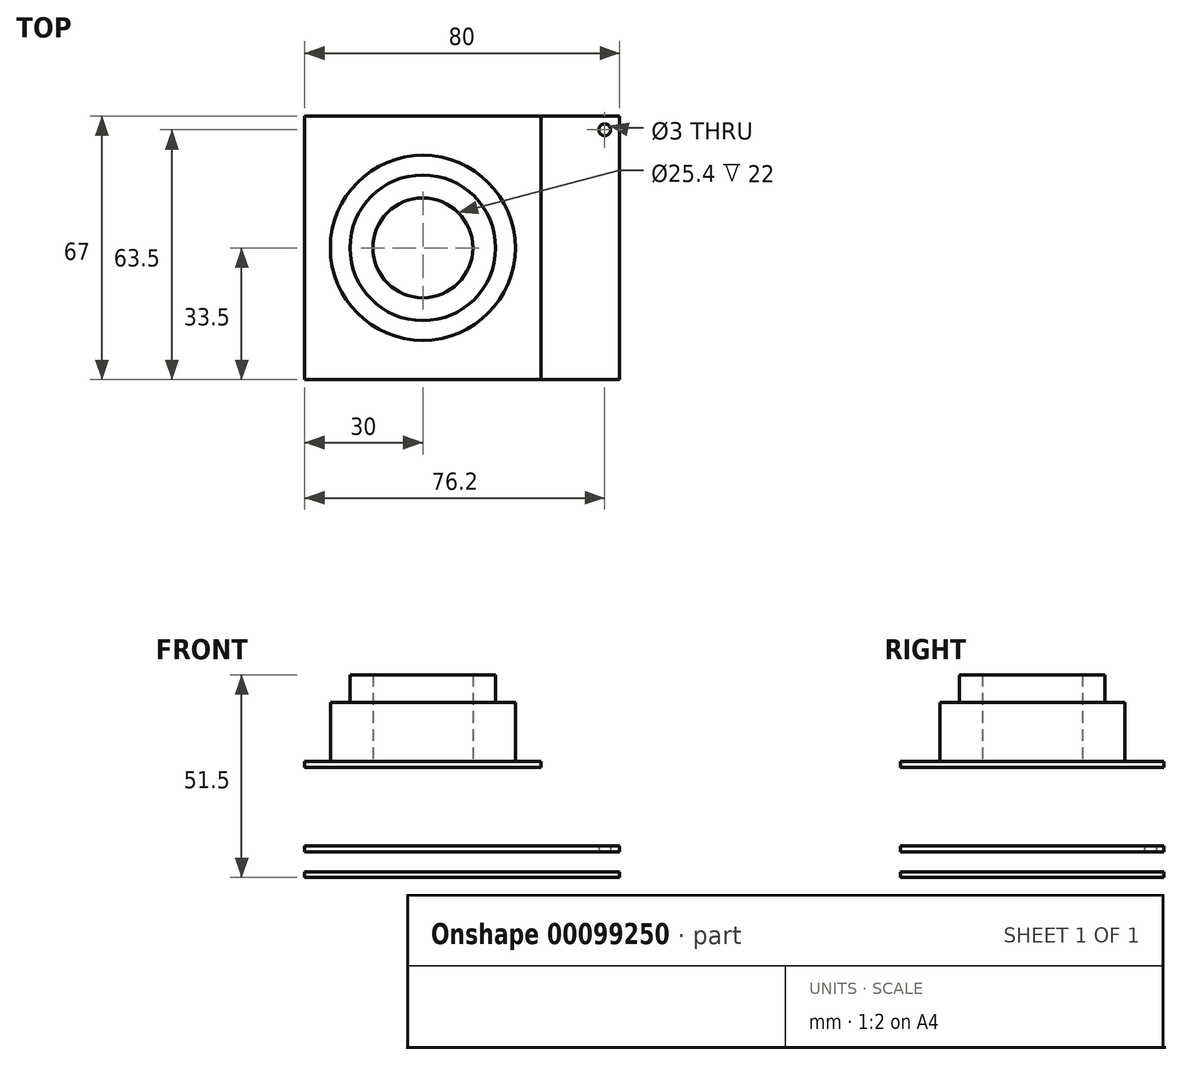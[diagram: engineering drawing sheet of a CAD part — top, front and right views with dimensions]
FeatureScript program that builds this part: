
annotation { "Feature Type Name" : "Feature", "Feature Type Description" : "" }
export const myFeature = defineFeature(function(context is Context, id is Id, definition is map)
    precondition{}
    {
        {
            var Q0;
            Q0=qCreatedBy(makeId("Top.planeOp"),FACE);
            var sketch = newSketch(context, id + "F0", { "sketchPlane" : qUnion([Q0])});
            skLineSegment(sketch, "E0.bottom", {"start": v(0, 0) * mm, "end": v(80, 0) * mm});
            skLineSegment(sketch, "E0.top", {"start": v(0, 67) * mm, "end": v(80, 67) * mm});
            skLineSegment(sketch, "E0.left", {"start": v(0, 0) * mm, "end": v(0, 67) * mm});
            skLineSegment(sketch, "E0.right", {"start": v(80, 0) * mm, "end": v(80, 67) * mm});
            skSolve(sketch);
        }
        {
            var Q0;
            Q0=makeQuery(id+"F0.imprint","IMPRINT",FACE,{"disambiguationData":[TD([[makeQuery(id+"F0.imprint","IMPRINT",EDGE,{"derivedFrom":sQuery(id+"F0.wireOp",EDGE,"E0.bottom")}),1.0]])]});
            extrude(context, id + "F1", {"entities" : qUnion([Q0]), "depth" : 1.5 * mm});
        }
        {
            var Q0;
            Q0=makeQuery(id+"F1.opExtrude","CAP_FACE",FACE,{"disambiguationData":[OSD([sQuery(id+"F0.wireOp",EDGE,"E0.bottom"),sQuery(id+"F0.wireOp",EDGE,"E0.top"),sQuery(id+"F0.wireOp",EDGE,"E0.left"),sQuery(id+"F0.wireOp",EDGE,"E0.right")])],"isStart":false});
            cPlane(context, id + "F2", {"entities" : qUnion([Q0]), "cplaneType" : CPlaneType.OFFSET, "offset" : 5 * mm, "width" : 150 * mm, "height" : 150 * mm});
        }
        {
            var Q0;
            Q0=qCreatedBy(id+"F2.planeOp",FACE);
            var sketch = newSketch(context, id + "F3", { "sketchPlane" : qUnion([Q0])});
            skLineSegment(sketch, "E1.bottom", {"start": v(0, 0) * mm, "end": v(80, 0) * mm});
            skLineSegment(sketch, "E1.top", {"start": v(0, 67) * mm, "end": v(80, 67) * mm});
            skLineSegment(sketch, "E1.left", {"start": v(0, 0) * mm, "end": v(0, 67) * mm});
            skLineSegment(sketch, "E1.right", {"start": v(80, 0) * mm, "end": v(80, 67) * mm});
            skCircle(sketch, "E2", {"center": v(76.2, 63.5) * mm, "radius": 1.5 * mm});
            skSolve(sketch);
        }
        {
            var Q0;
            Q0=makeQuery(id+"F3.imprint","IMPRINT",FACE,{"disambiguationData":[TD([[makeQuery(id+"F3.imprint","IMPRINT",EDGE,{"derivedFrom":sQuery(id+"F3.wireOp",EDGE,"E1.bottom")}),1.0]])]});
            extrude(context, id + "F4", {"entities" : qUnion([Q0]), "depth" : 1.5 * mm});
        }
        {
            var Q0;
            Q0=makeQuery(id+"F4.opExtrude","CAP_FACE",FACE,{"disambiguationData":[OSD([sQuery(id+"F3.wireOp",EDGE,"E1.bottom"),sQuery(id+"F3.wireOp",EDGE,"E1.top"),sQuery(id+"F3.wireOp",EDGE,"E1.left"),sQuery(id+"F3.wireOp",EDGE,"E1.right")])],"isStart":false});
            cPlane(context, id + "F5", {"entities" : qUnion([Q0]), "cplaneType" : CPlaneType.OFFSET, "offset" : 20 * mm, "width" : 150 * mm, "height" : 150 * mm});
        }
        {
            var Q0;
            Q0=qCreatedBy(id+"F5.planeOp",FACE);
            var sketch = newSketch(context, id + "F6", { "sketchPlane" : qUnion([Q0])});
            skLineSegment(sketch, "E3.bottom", {"start": v(0, 0) * mm, "end": v(60, 0) * mm});
            skLineSegment(sketch, "E3.top", {"start": v(0, 67) * mm, "end": v(60, 67) * mm});
            skLineSegment(sketch, "E3.left", {"start": v(0, 0) * mm, "end": v(0, 67) * mm});
            skLineSegment(sketch, "E3.right", {"start": v(60, 0) * mm, "end": v(60, 67) * mm});
            skSolve(sketch);
        }
        {
            var Q0;
            Q0=makeQuery(id+"F6.imprint","IMPRINT",FACE,{"disambiguationData":[TD([[makeQuery(id+"F6.imprint","IMPRINT",EDGE,{"derivedFrom":sQuery(id+"F6.wireOp",EDGE,"E3.bottom")}),1.0]])]});
            extrude(context, id + "F7", {"entities" : qUnion([Q0]), "depth" : 1.5 * mm});
        }
        {
            var Q0;
            Q0=makeQuery(id+"F7.opExtrude","CAP_FACE",FACE,{"disambiguationData":[OSD([sQuery(id+"F6.wireOp",EDGE,"E3.bottom"),sQuery(id+"F6.wireOp",EDGE,"E3.top"),sQuery(id+"F6.wireOp",EDGE,"E3.left"),sQuery(id+"F6.wireOp",EDGE,"E3.right")])],"isStart":false});
            var sketch = newSketch(context, id + "F8", { "sketchPlane" : qUnion([Q0])});
            skLineSegment(sketch, "E4", {"start": v(0, 33.5) * mm, "end": v(30, 33.5) * mm});
            skPoint(sketch, "E4.endSnap0", {"position": v(30, 67) * mm});
            skCircle(sketch, "E5", {"center": v(30, 33.5) * mm, "radius": 23.5 * mm});
            skCircle(sketch, "E6", {"center": v(30, 33.5) * mm, "radius": 18.5 * mm});
            skCircle(sketch, "E7", {"center": v(30, 33.5) * mm, "radius": 12.7 * mm});
            skSolve(sketch);
        }
        {
            var Q0;
            Q0=makeQuery(id+"F8.imprint","IMPRINT",FACE,{"disambiguationData":[TD([[makeQuery(id+"F8.imprint","IMPRINT",EDGE,{"derivedFrom":sQuery(id+"F8.wireOp",EDGE,"E6")}),1.0]])]});
            var Q1;
            Q1=makeQuery(id+"F8.imprint","IMPRINT",FACE,{"disambiguationData":[TD([[makeQuery(id+"F8.imprint","IMPRINT",EDGE,{"derivedFrom":sQuery(id+"F8.wireOp",EDGE,"E5")}),1.0]])]});
            extrude(context, id + "F9", {"entities" : qUnion([Q0, Q1]), "depth" : 15 * mm});
        }
        {
            var Q0;
            Q0=makeQuery(id+"F8.imprint","IMPRINT",FACE,{"disambiguationData":[TD([[makeQuery(id+"F8.imprint","IMPRINT",EDGE,{"derivedFrom":sQuery(id+"F8.wireOp",EDGE,"E6")}),1.0]])]});
            extrude(context, id + "F10", {"entities" : qUnion([Q0]), "operationType" : NewBodyOperationType.ADD, "depth" : 22 * mm});
        }
    });
